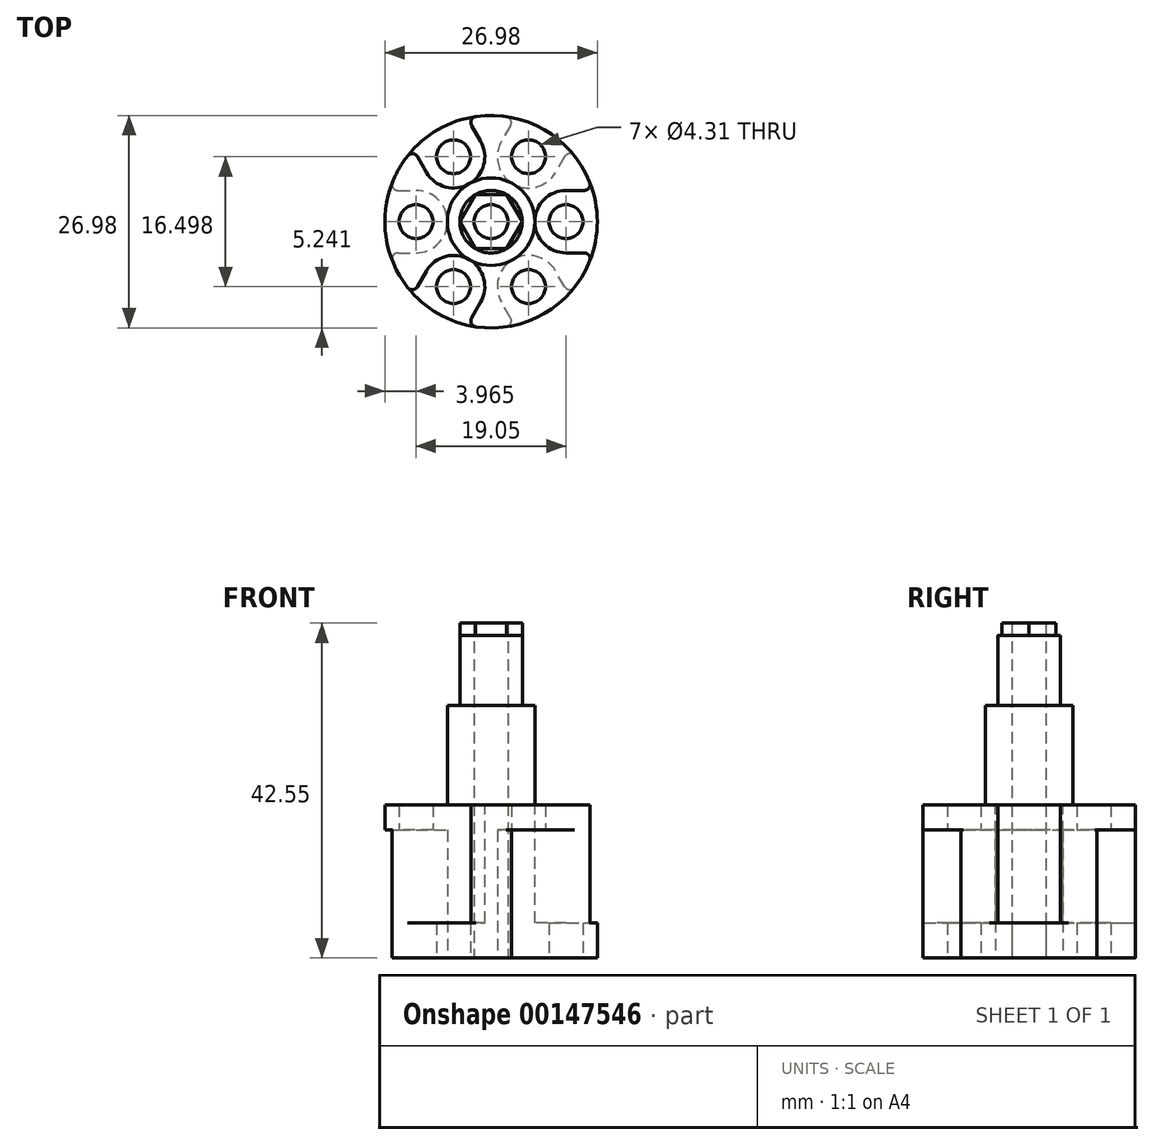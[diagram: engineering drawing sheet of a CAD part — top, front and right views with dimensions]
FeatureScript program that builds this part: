
annotation { "Feature Type Name" : "Feature", "Feature Type Description" : "" }
export const myFeature = defineFeature(function(context is Context, id is Id, definition is map)
    precondition{}
    {
        {
            var Q0;
            Q0=qCreatedBy(makeId("Top.planeOp"),FACE);
            var sketch = newSketch(context, id + "F0", { "sketchPlane" : qUnion([Q0])});
            skCircle(sketch, "E0", {"center": v(0, 0) * mm, "radius": 13.5 * mm});
            skCircle(sketch, "E1", {"center": v(4.76, -8.25) * mm, "radius": 3.97 * mm, "construction": true});
            skCircle(sketch, "E2", {"center": v(0, 0) * mm, "radius": 5.56 * mm, "construction": true});
            skCircle(sketch, "E3.cCircle", {"center": v(0, 0) * mm, "radius": 8.25 * mm, "construction": true});
            skLineSegment(sketch, "E3.0", {"start": v(-4.76, 8.25) * mm, "end": v(4.76, 8.25) * mm, "construction": true});
            skLineSegment(sketch, "E3.1", {"start": v(4.76, 8.25) * mm, "end": v(9.52, 0) * mm, "construction": true});
            skLineSegment(sketch, "E3.2", {"start": v(9.52, 0) * mm, "end": v(4.76, -8.25) * mm, "construction": true});
            skLineSegment(sketch, "E3.3", {"start": v(4.76, -8.25) * mm, "end": v(-4.76, -8.25) * mm, "construction": true});
            skLineSegment(sketch, "E3.4", {"start": v(-4.76, -8.25) * mm, "end": v(-9.52, 0) * mm, "construction": true});
            skLineSegment(sketch, "E3.5", {"start": v(-9.52, 0) * mm, "end": v(-4.76, 8.25) * mm, "construction": true});
            skPoint(sketch, "E3.0.midPoint", {"position": v(0, 8.25) * mm});
            skCircle(sketch, "E4", {"center": v(-4.76, -8.25) * mm, "radius": 2.15 * mm});
            skCircle(sketch, "E5", {"center": v(-9.52, 0) * mm, "radius": 2.15 * mm});
            skCircle(sketch, "E6", {"center": v(-4.76, 8.25) * mm, "radius": 2.15 * mm});
            skCircle(sketch, "E7", {"center": v(4.76, 8.25) * mm, "radius": 2.15 * mm});
            skCircle(sketch, "E8", {"center": v(9.52, 0) * mm, "radius": 2.15 * mm});
            skCircle(sketch, "E9", {"center": v(4.76, -8.25) * mm, "radius": 2.15 * mm});
            skCircle(sketch, "E10", {"center": v(0, 0) * mm, "radius": 2.15 * mm});
            skSolve(sketch);
        }
        {
            var Q0;
            Q0=qSketchRegion(id+"F0",true);
            extrude(context, id + "F1", {"entities" : qUnion([Q0]), "depth" : 19.42 * mm});
        }
        {
            var Q0;
            Q0=makeQuery(id+"F1.opExtrude","CAP_FACE",FACE,{"disambiguationData":[OSD([sQuery(id+"F0.wireOp",EDGE,"E0"),sQuery(id+"F0.wireOp",EDGE,"E4"),sQuery(id+"F0.wireOp",EDGE,"E5"),sQuery(id+"F0.wireOp",EDGE,"E6"),sQuery(id+"F0.wireOp",EDGE,"E7"),sQuery(id+"F0.wireOp",EDGE,"E8"),sQuery(id+"F0.wireOp",EDGE,"E9")])],"isStart":false});
            cPlane(context, id + "F2", {"entities" : qUnion([Q0]), "cplaneType" : CPlaneType.OFFSET, "offset" : 3.17 * mm, "oppositeDirection" : true, "width" : 152.4 * mm, "height" : 152.4 * mm});
        }
        {
            var Q0;
            Q0=makeQuery(id+"F1.opExtrude","CAP_FACE",FACE,{"disambiguationData":[OSD([sQuery(id+"F0.wireOp",EDGE,"E0"),sQuery(id+"F0.wireOp",EDGE,"E4"),sQuery(id+"F0.wireOp",EDGE,"E5"),sQuery(id+"F0.wireOp",EDGE,"E6"),sQuery(id+"F0.wireOp",EDGE,"E7"),sQuery(id+"F0.wireOp",EDGE,"E8"),sQuery(id+"F0.wireOp",EDGE,"E9")])],"isStart":true});
            cPlane(context, id + "F3", {"entities" : qUnion([Q0]), "cplaneType" : CPlaneType.OFFSET, "offset" : 4.44 * mm, "oppositeDirection" : true, "width" : 152.4 * mm, "height" : 152.4 * mm});
        }
        {
            var Q0;
            Q0=makeQuery(id+"F1.opExtrude","CAP_FACE",FACE,{"disambiguationData":[OSD([sQuery(id+"F0.wireOp",EDGE,"E0"),sQuery(id+"F0.wireOp",EDGE,"E4"),sQuery(id+"F0.wireOp",EDGE,"E5"),sQuery(id+"F0.wireOp",EDGE,"E6"),sQuery(id+"F0.wireOp",EDGE,"E7"),sQuery(id+"F0.wireOp",EDGE,"E8"),sQuery(id+"F0.wireOp",EDGE,"E9")])],"isStart":false});
            var sketch = newSketch(context, id + "F4", { "sketchPlane" : qUnion([Q0])});
            skLineSegment(sketch, "E11", {"start": v(-4.76, 8.25) * mm, "end": v(0, 0) * mm, "construction": true});
            skLineSegment(sketch, "E12", {"start": v(9.52, 0) * mm, "end": v(0, 0) * mm, "construction": true});
            skLineSegment(sketch, "E13", {"start": v(0, 0) * mm, "end": v(-4.76, -8.25) * mm, "construction": true});
            skLineSegment(sketch, "E14.bottom", {"start": v(-8.2, 6.26) * mm, "end": v(-1.33, 10.23) * mm, "construction": true});
            skLineSegment(sketch, "E14.top", {"start": v(-10.18, 9.7) * mm, "end": v(-3.3, 13.67) * mm});
            skLineSegment(sketch, "E14.left", {"start": v(-8.2, 6.26) * mm, "end": v(-10.18, 9.7) * mm});
            skLineSegment(sketch, "E14.right", {"start": v(-1.33, 10.23) * mm, "end": v(-3.3, 13.67) * mm});
            skLineSegment(sketch, "E15.bottom", {"start": v(9.52, 3.97) * mm, "end": v(13.5, 3.97) * mm});
            skLineSegment(sketch, "E15.top", {"start": v(9.52, -3.97) * mm, "end": v(13.5, -3.97) * mm});
            skLineSegment(sketch, "E15.left", {"start": v(9.52, 3.97) * mm, "end": v(9.52, -3.97) * mm, "construction": true});
            skLineSegment(sketch, "E15.right", {"start": v(13.5, 3.97) * mm, "end": v(13.5, -3.97) * mm});
            skLineSegment(sketch, "E16.bottom", {"start": v(-8.2, -6.26) * mm, "end": v(-1.33, -10.23) * mm, "construction": true});
            skLineSegment(sketch, "E16.top", {"start": v(-10.18, -9.7) * mm, "end": v(-3.3, -13.67) * mm});
            skLineSegment(sketch, "E16.left", {"start": v(-8.2, -6.26) * mm, "end": v(-10.18, -9.7) * mm});
            skLineSegment(sketch, "E16.right", {"start": v(-1.33, -10.23) * mm, "end": v(-3.3, -13.67) * mm});
            skArc(sketch, "E17", {"start": v(-1.33, -10.23) * mm, "mid": v(-2.78, -4.81) * mm, "end": v(-8.2, -6.26) * mm});
            skArc(sketch, "E18", {"start": v(9.52, 3.97) * mm, "mid": v(5.56, 0) * mm, "end": v(9.52, -3.97) * mm});
            skArc(sketch, "E19", {"start": v(-8.2, 6.26) * mm, "mid": v(-2.78, 4.81) * mm, "end": v(-1.33, 10.23) * mm});
            skSolve(sketch);
        }
        {
            var Q0;
            Q0=qSketchRegion(id+"F4",true);
            var Q1;
            Q1=qCreatedBy(id+"F3.planeOp",FACE);
            extrude(context, id + "F5", {"entities" : qUnion([Q0]), "operationType" : NewBodyOperationType.REMOVE, "endBound" : BoundingType.UP_TO_SURFACE, "oppositeDirection" : true, "endBoundEntityFace" : qUnion([Q1]), "depth" : 25.4 * mm});
        }
        {
            var Q0;
            Q0=makeQuery(id+"F1.opExtrude","CAP_FACE",FACE,{"disambiguationData":[OSD([sQuery(id+"F0.wireOp",EDGE,"E0"),sQuery(id+"F0.wireOp",EDGE,"E4"),sQuery(id+"F0.wireOp",EDGE,"E5"),sQuery(id+"F0.wireOp",EDGE,"E6"),sQuery(id+"F0.wireOp",EDGE,"E7"),sQuery(id+"F0.wireOp",EDGE,"E8"),sQuery(id+"F0.wireOp",EDGE,"E9"),sQuery(id+"F0.wireOp",EDGE,"E10")])],"isStart":true});
            var sketch = newSketch(context, id + "F6", { "sketchPlane" : qUnion([Q0])});
            skLineSegment(sketch, "E20", {"start": v(0, 0) * mm, "end": v(-9.52, 0) * mm, "construction": true});
            skLineSegment(sketch, "E21", {"start": v(0, 0) * mm, "end": v(4.76, 8.25) * mm, "construction": true});
            skLineSegment(sketch, "E22", {"start": v(0, 0) * mm, "end": v(4.76, -8.25) * mm, "construction": true});
            skLineSegment(sketch, "E23.bottom", {"start": v(3.3, -13.67) * mm, "end": v(10.18, -9.7) * mm});
            skLineSegment(sketch, "E23.top", {"start": v(1.33, -10.23) * mm, "end": v(8.2, -6.26) * mm, "construction": true});
            skLineSegment(sketch, "E23.left", {"start": v(3.3, -13.67) * mm, "end": v(1.33, -10.23) * mm});
            skLineSegment(sketch, "E23.right", {"start": v(10.18, -9.7) * mm, "end": v(8.2, -6.26) * mm});
            skLineSegment(sketch, "E24.bottom", {"start": v(3.3, 13.67) * mm, "end": v(10.18, 9.7) * mm});
            skLineSegment(sketch, "E24.top", {"start": v(1.33, 10.23) * mm, "end": v(8.2, 6.26) * mm, "construction": true});
            skLineSegment(sketch, "E24.left", {"start": v(3.3, 13.67) * mm, "end": v(1.33, 10.23) * mm});
            skLineSegment(sketch, "E24.right", {"start": v(10.18, 9.7) * mm, "end": v(8.2, 6.26) * mm});
            skLineSegment(sketch, "E25.bottom", {"start": v(-13.5, 3.97) * mm, "end": v(-9.52, 3.97) * mm});
            skLineSegment(sketch, "E25.top", {"start": v(-13.5, -3.97) * mm, "end": v(-9.52, -3.97) * mm});
            skLineSegment(sketch, "E25.left", {"start": v(-13.5, 3.97) * mm, "end": v(-13.5, -3.97) * mm});
            skLineSegment(sketch, "E25.right", {"start": v(-9.52, 3.97) * mm, "end": v(-9.52, -3.97) * mm, "construction": true});
            skArc(sketch, "E26", {"start": v(8.2, -6.26) * mm, "mid": v(2.78, -4.81) * mm, "end": v(1.33, -10.23) * mm});
            skArc(sketch, "E27", {"start": v(1.33, 10.23) * mm, "mid": v(2.78, 4.81) * mm, "end": v(8.2, 6.26) * mm});
            skArc(sketch, "E28", {"start": v(-9.52, -3.97) * mm, "mid": v(-5.56, 0) * mm, "end": v(-9.52, 3.97) * mm});
            skSolve(sketch);
        }
        {
            var Q0;
            Q0=qSketchRegion(id+"F6",true);
            var Q1;
            Q1=qCreatedBy(id+"F2.planeOp",FACE);
            extrude(context, id + "F7", {"entities" : qUnion([Q0]), "operationType" : NewBodyOperationType.REMOVE, "endBound" : BoundingType.UP_TO_SURFACE, "oppositeDirection" : true, "endBoundEntityFace" : qUnion([Q1]), "depth" : 25.4 * mm});
        }
        {
            var Q0;
            Q0=makeQuery(id+"F1.opExtrude","CAP_FACE",FACE,{"disambiguationData":[OSD([sQuery(id+"F0.wireOp",EDGE,"E0"),sQuery(id+"F0.wireOp",EDGE,"E4"),sQuery(id+"F0.wireOp",EDGE,"E5"),sQuery(id+"F0.wireOp",EDGE,"E6"),sQuery(id+"F0.wireOp",EDGE,"E7"),sQuery(id+"F0.wireOp",EDGE,"E8"),sQuery(id+"F0.wireOp",EDGE,"E9"),sQuery(id+"F0.wireOp",EDGE,"E10")])],"isStart":false});
            var sketch = newSketch(context, id + "F8", { "sketchPlane" : qUnion([Q0])});
            skCircle(sketch, "E29", {"center": v(0, 0) * mm, "radius": 5.56 * mm});
            skCircle(sketch, "E30", {"center": v(0, 0) * mm, "radius": 2.15 * mm});
            skSolve(sketch);
        }
        {
            var Q0;
            Q0=qSketchRegion(id+"F8",true);
            extrude(context, id + "F9", {"entities" : qUnion([Q0]), "operationType" : NewBodyOperationType.ADD, "depth" : 12.65 * mm});
        }
        {
            var Q0;
            Q0=makeQuery(id+"F9.opExtrude","CAP_FACE",FACE,{"disambiguationData":[OSD([sQuery(id+"F8.wireOp",EDGE,"E29"),sQuery(id+"F8.wireOp",EDGE,"E30")])],"isStart":false});
            var sketch = newSketch(context, id + "F10", { "sketchPlane" : qUnion([Q0])});
            skCircle(sketch, "E31", {"center": v(0, 0) * mm, "radius": 3.97 * mm});
            skCircle(sketch, "E32", {"center": v(0, 0) * mm, "radius": 2.15 * mm});
            skSolve(sketch);
        }
        {
            var Q0;
            Q0=qSketchRegion(id+"F10",true);
            extrude(context, id + "F11", {"entities" : qUnion([Q0]), "operationType" : NewBodyOperationType.ADD, "depth" : 8.9 * mm});
        }
        {
            var Q0;
            Q0=makeQuery(id+"F11.opExtrude","CAP_FACE",FACE,{"disambiguationData":[OSD([sQuery(id+"F10.wireOp",EDGE,"E31"),sQuery(id+"F10.wireOp",EDGE,"E32")])],"isStart":false});
            var sketch = newSketch(context, id + "F12", { "sketchPlane" : qUnion([Q0])});
            skCircle(sketch, "E33.cCircle", {"center": v(0, 0) * mm, "radius": 3.97 * mm, "construction": true});
            skLineSegment(sketch, "E33.0", {"start": v(-1.98, 3.44) * mm, "end": v(1.98, 3.44) * mm});
            skLineSegment(sketch, "E33.1", {"start": v(1.98, 3.44) * mm, "end": v(3.97, 0) * mm});
            skLineSegment(sketch, "E33.2", {"start": v(3.97, 0) * mm, "end": v(1.98, -3.44) * mm});
            skLineSegment(sketch, "E33.3", {"start": v(1.98, -3.44) * mm, "end": v(-1.98, -3.44) * mm});
            skLineSegment(sketch, "E33.4", {"start": v(-1.98, -3.44) * mm, "end": v(-3.97, 0) * mm});
            skLineSegment(sketch, "E33.5", {"start": v(-3.97, 0) * mm, "end": v(-1.98, 3.44) * mm});
            skCircle(sketch, "E34", {"center": v(0, 0) * mm, "radius": 2.15 * mm});
            skSolve(sketch);
        }
        {
            var Q0;
            Q0=qSketchRegion(id+"F12",true);
            extrude(context, id + "F13", {"entities" : qUnion([Q0]), "operationType" : NewBodyOperationType.ADD, "depth" : 1.59 * mm});
        }
        {
            var Q0;
            Q0=makeQuery(id+"F5.boolean.opBoolean","INTERSECT",EDGE,{"derivedFrom":[makeQuery(id+"F1.opExtrude","SWEPT_FACE",FACE,{"disambiguationData":[OSD([sQuery(id+"F0.wireOp",EDGE,"E0")])]}),makeQuery(id+"F5.opExtrude","SWEPT_FACE",FACE,{"disambiguationData":[OSD([sQuery(id+"F4.wireOp",EDGE,"E16.left")])]})]});
            var Q1;
            Q1=makeQuery(id+"F7.boolean.opBoolean","INTERSECT",EDGE,{"derivedFrom":[makeQuery(id+"F1.opExtrude","SWEPT_FACE",FACE,{"disambiguationData":[OSD([sQuery(id+"F0.wireOp",EDGE,"E0")])]}),makeQuery(id+"F7.opExtrude","SWEPT_FACE",FACE,{"disambiguationData":[OSD([sQuery(id+"F6.wireOp",EDGE,"E24.left")])]})]});
            var Q2;
            Q2=makeQuery(id+"F7.boolean.opBoolean","INTERSECT",EDGE,{"derivedFrom":[makeQuery(id+"F1.opExtrude","SWEPT_FACE",FACE,{"disambiguationData":[OSD([sQuery(id+"F0.wireOp",EDGE,"E0")])]}),makeQuery(id+"F7.opExtrude","SWEPT_FACE",FACE,{"disambiguationData":[OSD([sQuery(id+"F6.wireOp",EDGE,"E24.right")])]})]});
            var Q3;
            Q3=makeQuery(id+"F5.boolean.opBoolean","INTERSECT",EDGE,{"derivedFrom":[makeQuery(id+"F1.opExtrude","SWEPT_FACE",FACE,{"disambiguationData":[OSD([sQuery(id+"F0.wireOp",EDGE,"E0")])]}),makeQuery(id+"F5.opExtrude","SWEPT_FACE",FACE,{"disambiguationData":[OSD([sQuery(id+"F4.wireOp",EDGE,"E15.bottom")])]})]});
            var Q4;
            Q4=makeQuery(id+"F5.boolean.opBoolean","INTERSECT",EDGE,{"derivedFrom":[makeQuery(id+"F1.opExtrude","SWEPT_FACE",FACE,{"disambiguationData":[OSD([sQuery(id+"F0.wireOp",EDGE,"E0")])]}),makeQuery(id+"F5.opExtrude","SWEPT_FACE",FACE,{"disambiguationData":[OSD([sQuery(id+"F4.wireOp",EDGE,"E15.top")])]})]});
            var Q5;
            Q5=makeQuery(id+"F5.boolean.opBoolean","INTERSECT",EDGE,{"derivedFrom":[makeQuery(id+"F1.opExtrude","SWEPT_FACE",FACE,{"disambiguationData":[OSD([sQuery(id+"F0.wireOp",EDGE,"E0")])]}),makeQuery(id+"F5.opExtrude","SWEPT_FACE",FACE,{"disambiguationData":[OSD([sQuery(id+"F4.wireOp",EDGE,"E16.right")])]})]});
            var Q6;
            Q6=makeQuery(id+"F7.boolean.opBoolean","INTERSECT",EDGE,{"derivedFrom":[makeQuery(id+"F1.opExtrude","SWEPT_FACE",FACE,{"disambiguationData":[OSD([sQuery(id+"F0.wireOp",EDGE,"E0")])]}),makeQuery(id+"F7.opExtrude","SWEPT_FACE",FACE,{"disambiguationData":[OSD([sQuery(id+"F6.wireOp",EDGE,"E23.right")])]})]});
            var Q7;
            Q7=makeQuery(id+"F7.boolean.opBoolean","INTERSECT",EDGE,{"derivedFrom":[makeQuery(id+"F1.opExtrude","SWEPT_FACE",FACE,{"disambiguationData":[OSD([sQuery(id+"F0.wireOp",EDGE,"E0")])]}),makeQuery(id+"F7.opExtrude","SWEPT_FACE",FACE,{"disambiguationData":[OSD([sQuery(id+"F6.wireOp",EDGE,"E23.left")])]})]});
            var Q8;
            Q8=makeQuery(id+"F5.boolean.opBoolean","INTERSECT",EDGE,{"derivedFrom":[makeQuery(id+"F1.opExtrude","SWEPT_FACE",FACE,{"disambiguationData":[OSD([sQuery(id+"F0.wireOp",EDGE,"E0")])]}),makeQuery(id+"F5.opExtrude","SWEPT_FACE",FACE,{"disambiguationData":[OSD([sQuery(id+"F4.wireOp",EDGE,"E14.right")])]})]});
            var Q9;
            Q9=makeQuery(id+"F5.boolean.opBoolean","INTERSECT",EDGE,{"derivedFrom":[makeQuery(id+"F1.opExtrude","SWEPT_FACE",FACE,{"disambiguationData":[OSD([sQuery(id+"F0.wireOp",EDGE,"E0")])]}),makeQuery(id+"F5.opExtrude","SWEPT_FACE",FACE,{"disambiguationData":[OSD([sQuery(id+"F4.wireOp",EDGE,"E14.left")])]})]});
            var Q10;
            Q10=makeQuery(id+"F7.boolean.opBoolean","INTERSECT",EDGE,{"derivedFrom":[makeQuery(id+"F1.opExtrude","SWEPT_FACE",FACE,{"disambiguationData":[OSD([sQuery(id+"F0.wireOp",EDGE,"E0")])]}),makeQuery(id+"F7.opExtrude","SWEPT_FACE",FACE,{"disambiguationData":[OSD([sQuery(id+"F6.wireOp",EDGE,"E25.top")])]})]});
            var Q11;
            Q11=makeQuery(id+"F7.boolean.opBoolean","INTERSECT",EDGE,{"derivedFrom":[makeQuery(id+"F1.opExtrude","SWEPT_FACE",FACE,{"disambiguationData":[OSD([sQuery(id+"F0.wireOp",EDGE,"E0")])]}),makeQuery(id+"F7.opExtrude","SWEPT_FACE",FACE,{"disambiguationData":[OSD([sQuery(id+"F6.wireOp",EDGE,"E25.bottom")])]})]});
            fillet(context, id + "F14", {"entities" : qUnion([Q0, Q1, Q2, Q3, Q4, Q5, Q6, Q7, Q8, Q9, Q10, Q11]), "radius" : 0.76 * mm, "tangentPropagation" : true, "allowEdgeOverflow" : false});
        }
    });
